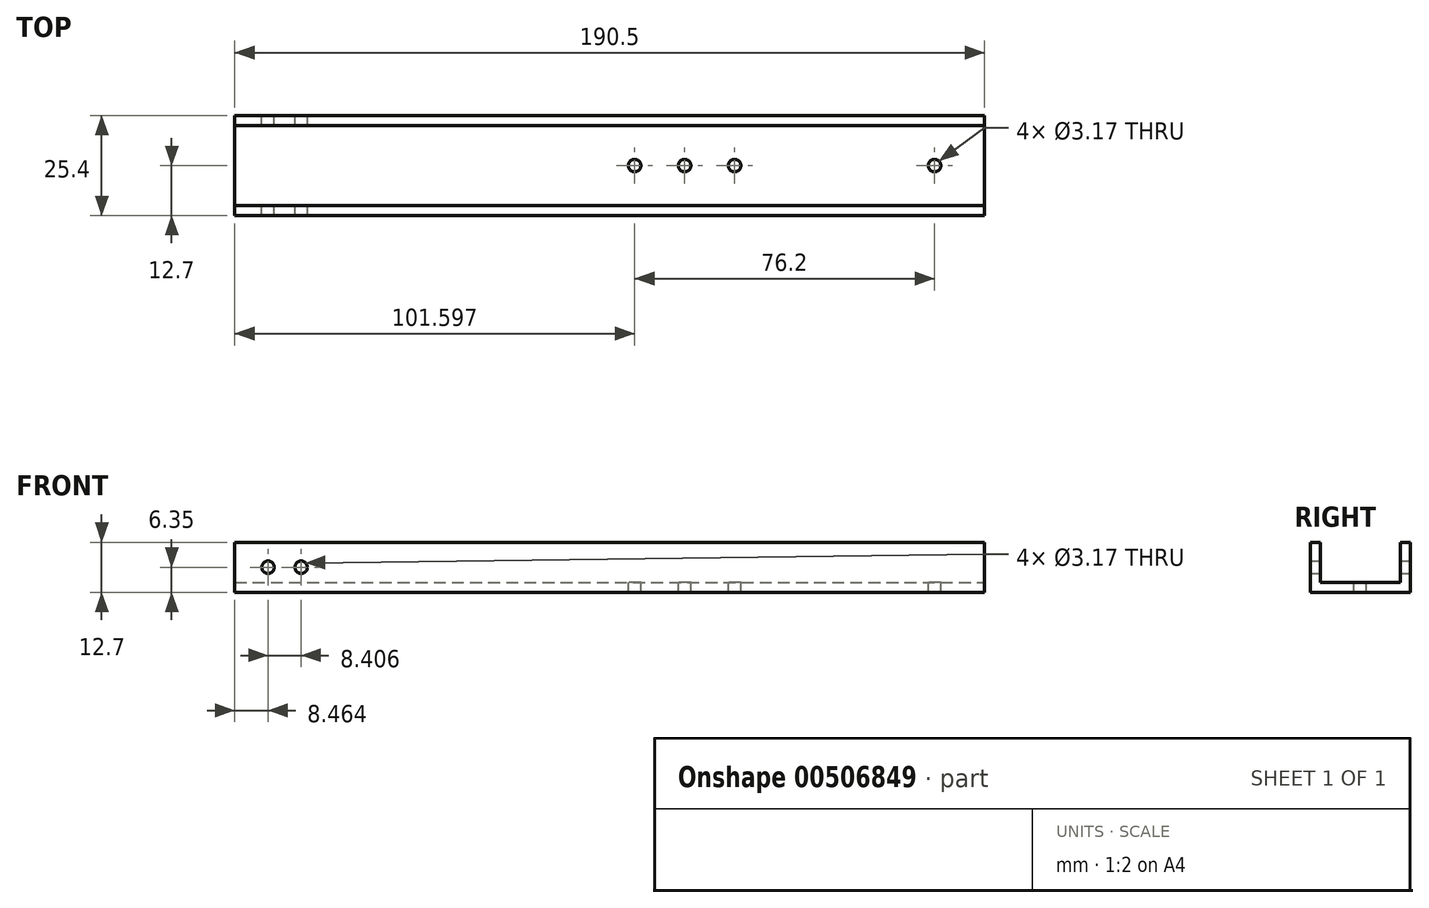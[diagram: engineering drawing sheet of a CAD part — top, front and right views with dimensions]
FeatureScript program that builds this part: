
annotation { "Feature Type Name" : "Feature", "Feature Type Description" : "" }
export const myFeature = defineFeature(function(context is Context, id is Id, definition is map)
    precondition{}
    {
        {
            var Q0;
            Q0=qCreatedBy(makeId("Top.planeOp"),FACE);
            var sketch = newSketch(context, id + "F0", { "sketchPlane" : qUnion([Q0])});
            skLineSegment(sketch, "E0.bottom", {"start": v(-91.18, 25.4) * mm, "end": v(99.32, 25.4) * mm});
            skLineSegment(sketch, "E0.top", {"start": v(-91.18, 0) * mm, "end": v(99.32, 0) * mm});
            skLineSegment(sketch, "E0.left", {"start": v(-91.18, 25.4) * mm, "end": v(-91.18, 0) * mm});
            skLineSegment(sketch, "E0.right", {"start": v(99.32, 25.4) * mm, "end": v(99.32, 0) * mm});
            skSolve(sketch);
        }
        {
            var Q0;
            Q0=makeQuery(id+"F0.imprint","IMPRINT",FACE,{"disambiguationData":[TD([[makeQuery(id+"F0.imprint","IMPRINT",EDGE,{"derivedFrom":sQuery(id+"F0.wireOp",EDGE,"E0.bottom")}),-1.0]])]});
            extrude(context, id + "F1", {"entities" : qUnion([Q0]), "depth" : 12.7 * mm, "offsetDistance" : 25.4 * mm});
        }
        {
            var Q0;
            Q0=makeQuery(id+"F1.opExtrude","CAP_FACE",FACE,{"disambiguationData":[OSD([sQuery(id+"F0.wireOp",EDGE,"E0.bottom"),sQuery(id+"F0.wireOp",EDGE,"E0.top"),sQuery(id+"F0.wireOp",EDGE,"E0.left"),sQuery(id+"F0.wireOp",EDGE,"E0.right")])],"isStart":false});
            var Q1;
            Q1=makeQuery(id+"F1.opExtrude","SWEPT_FACE",FACE,{"disambiguationData":[OSD([sQuery(id+"F0.wireOp",EDGE,"E0.right")])]});
            var Q2;
            Q2=makeQuery(id+"F1.opExtrude","SWEPT_FACE",FACE,{"disambiguationData":[OSD([sQuery(id+"F0.wireOp",EDGE,"E0.left")])]});
            shell(context, id + "F2", {"entities" : qUnion([Q0, Q1, Q2]), "thickness" : 2.54 * mm});
        }
        {
            var Q0;
            {var subQ0=sQuery(id+"F0.wireOp",EDGE,"E0.right");var subQ1=sQuery(id+"F0.wireOp",EDGE,"E0.left");var subQ2=sQuery(id+"F0.wireOp",EDGE,"E0.top");var subQ3=sQuery(id+"F0.wireOp",EDGE,"E0.bottom");Q0=makeQuery(id+"F2.opShell","OFFSET_FACE",FACE,{"disambiguationData":[OSD([subQ3,subQ2,subQ1,subQ0]),TDD([makeQuery(id+"F1.opExtrude","CAP_FACE",FACE,{"disambiguationData":[OSD([subQ3,subQ2,subQ1,subQ0])],"isStart":true})])]});}
            var sketch = newSketch(context, id + "F3", { "sketchPlane" : qUnion([Q0])});
            skPoint(sketch, "E1", {"position": v(86.62, 12.7) * mm});
            skPoint(sketch, "E1.positionSnap0", {"position": v(99.32, 12.7) * mm});
            skPoint(sketch, "E2", {"position": v(35.82, 12.7) * mm});
            skPoint(sketch, "E3", {"position": v(23.12, 12.7) * mm});
            skPoint(sketch, "E4", {"position": v(10.42, 12.7) * mm});
            skSolve(sketch);
        }
        {
            var Q0;
            Q0=sQuery(id+"F3.wireOp",VERTEX,"E4");
            var Q1;
            Q1=sQuery(id+"F3.wireOp",VERTEX,"E3");
            var Q2;
            Q2=sQuery(id+"F3.wireOp",VERTEX,"E2");
            var Q3;
            Q3=sQuery(id+"F3.wireOp",VERTEX,"E1");
            var Q4;
            Q4=makeQuery(id+"F1.opExtrude","SWEPT_BODY",BODY,{"disambiguationData":[OSD([sQuery(id+"F0.wireOp",EDGE,"E0.bottom"),sQuery(id+"F0.wireOp",EDGE,"E0.top"),sQuery(id+"F0.wireOp",EDGE,"E0.left"),sQuery(id+"F0.wireOp",EDGE,"E0.right")])]});
            hole(context, id + "F4", {"style" : HoleStyle.SIMPLE, "endStyle" : HoleEndStyle.THROUGH, "holeDiameter" : 3.17 * mm, "majorDiameter" : 6.35 * mm, "isTappedThrough" : true, "tappedDepth" : 12.7 * mm, "tapClearance" : 3, "locations" : qUnion([Q0, Q1, Q2, Q3]), "scope" : qUnion([Q4])});
        }
        {
            var Q0;
            Q0=makeQuery(id+"F1.opExtrude","SWEPT_FACE",FACE,{"disambiguationData":[OSD([sQuery(id+"F0.wireOp",EDGE,"E0.bottom")])]});
            var sketch = newSketch(context, id + "F5", { "sketchPlane" : qUnion([Q0])});
            skPoint(sketch, "E5", {"position": v(82.72, 6.35) * mm});
            skPoint(sketch, "E6", {"position": v(74.31, 6.35) * mm});
            skSolve(sketch);
        }
        {
            var Q0;
            Q0=sQuery(id+"F5.wireOp",VERTEX,"E6");
            var Q1;
            Q1=sQuery(id+"F5.wireOp",VERTEX,"E5");
            var Q2;
            Q2=makeQuery(id+"F1.opExtrude","SWEPT_BODY",BODY,{"disambiguationData":[OSD([sQuery(id+"F0.wireOp",EDGE,"E0.bottom"),sQuery(id+"F0.wireOp",EDGE,"E0.top"),sQuery(id+"F0.wireOp",EDGE,"E0.left"),sQuery(id+"F0.wireOp",EDGE,"E0.right")])]});
            hole(context, id + "F6", {"style" : HoleStyle.SIMPLE, "endStyle" : HoleEndStyle.THROUGH, "holeDiameter" : 3.17 * mm, "majorDiameter" : 6.35 * mm, "isTappedThrough" : true, "tappedDepth" : 12.7 * mm, "tapClearance" : 3, "locations" : qUnion([Q0, Q1]), "scope" : qUnion([Q2])});
        }
    });
